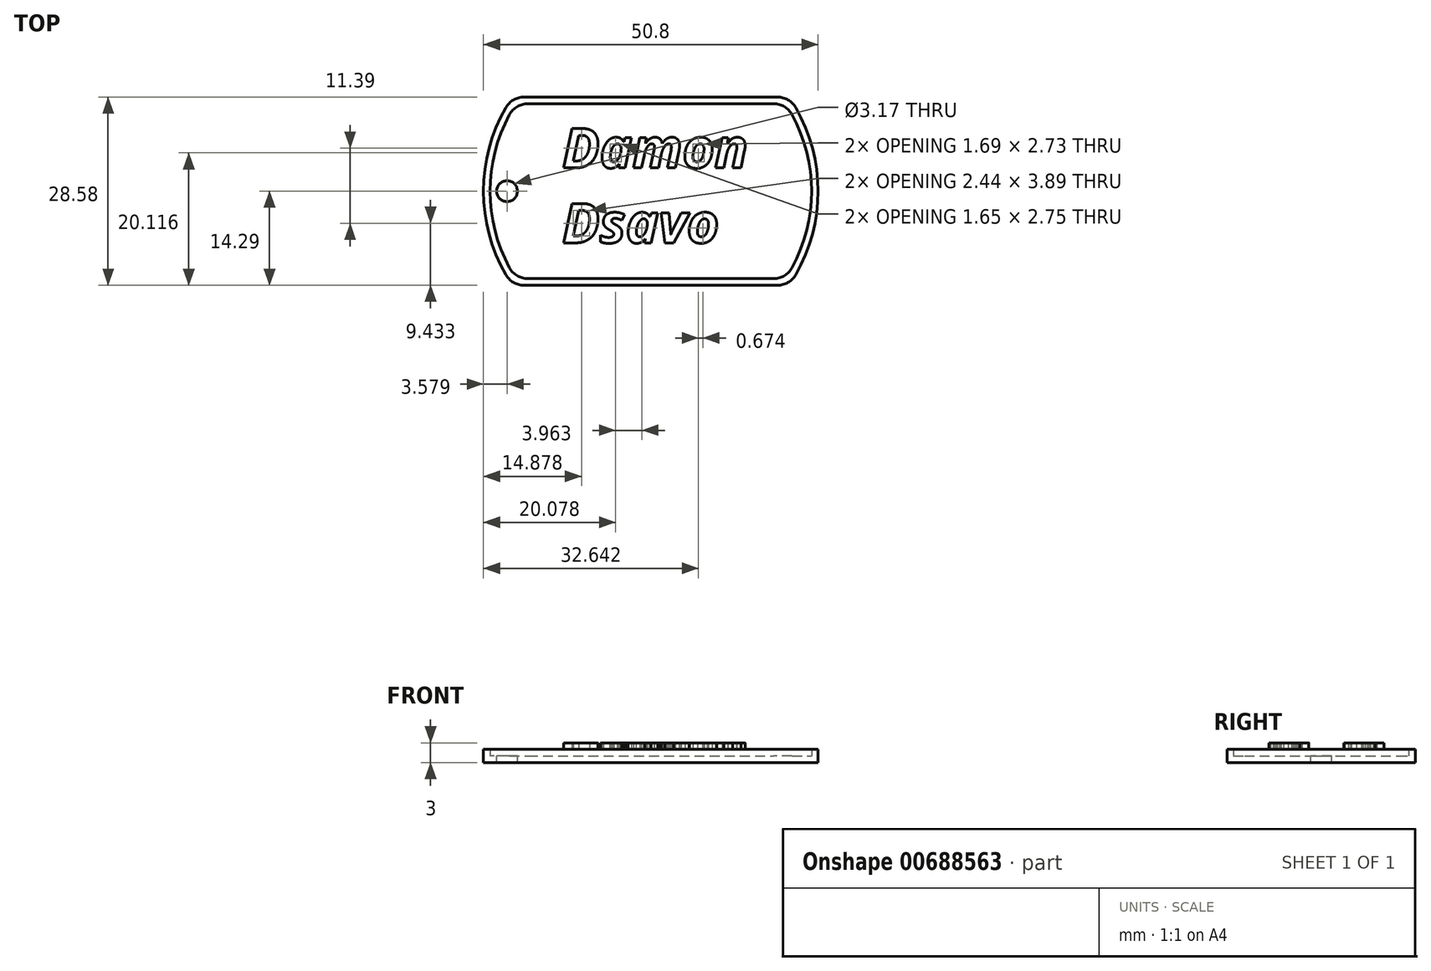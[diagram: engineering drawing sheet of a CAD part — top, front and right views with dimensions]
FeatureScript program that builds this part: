
annotation { "Feature Type Name" : "Feature", "Feature Type Description" : "" }
export const myFeature = defineFeature(function(context is Context, id is Id, definition is map)
    precondition{}
    {
        {
            var Q0;
            Q0=qCreatedBy(makeId("Top.planeOp"),FACE);
            var sketch = newSketch(context, id + "F0", { "sketchPlane" : qUnion([Q0])});
            skArc(sketch, "E0", {"start": v(-22, 12.7) * mm, "mid": v(-25.4, 0) * mm, "end": v(-22, -12.7) * mm});
            skLineSegment(sketch, "E1.top", {"start": v(-19.25, -14.29) * mm, "end": v(19.25, -14.29) * mm});
            skArc(sketch, "E2.trimOffspring", {"start": v(22, -12.7) * mm, "mid": v(25.4, 0) * mm, "end": v(22, 12.7) * mm});
            skLineSegment(sketch, "E3", {"start": v(-19.25, 14.29) * mm, "end": v(19.25, 14.29) * mm});
            skPoint(sketch, "E4.visualSharp", {"position": v(-21, 14.29) * mm});
            skArc(sketch, "E4.filletArc", {"start": v(-19.25, 14.29) * mm, "mid": v(-20.83, 13.86) * mm, "end": v(-22, 12.7) * mm});
            skPoint(sketch, "E5.visualSharp", {"position": v(21, 14.29) * mm});
            skArc(sketch, "E5.filletArc", {"start": v(22, 12.7) * mm, "mid": v(20.83, 13.86) * mm, "end": v(19.25, 14.29) * mm});
            skPoint(sketch, "E6.visualSharp", {"position": v(21, -14.29) * mm});
            skArc(sketch, "E6.filletArc", {"start": v(19.25, -14.29) * mm, "mid": v(20.83, -13.86) * mm, "end": v(22, -12.7) * mm});
            skPoint(sketch, "E7.visualSharp", {"position": v(-21, -14.29) * mm});
            skArc(sketch, "E7.filletArc", {"start": v(-22, -12.7) * mm, "mid": v(-20.83, -13.86) * mm, "end": v(-19.25, -14.29) * mm});
            skSolve(sketch);
        }
        {
            var Q0;
            Q0=makeQuery(id+"F0.imprint","IMPRINT",FACE,{"disambiguationData":[TD([[makeQuery(id+"F0.imprint","IMPRINT",EDGE,{"derivedFrom":sQuery(id+"F0.wireOp",EDGE,"E0")}),1.0]])]});
            extrude(context, id + "F1", {"entities" : qUnion([Q0]), "depth" : 1 * mm, "offsetDistance" : 25.4 * mm});
        }
        {
            var Q0;
            Q0=makeQuery(id+"F1.opExtrude","CAP_FACE",FACE,{"disambiguationData":[OSD([sQuery(id+"F0.wireOp",EDGE,"E0"),sQuery(id+"F0.wireOp",EDGE,"E1.top"),sQuery(id+"F0.wireOp",EDGE,"E2.trimOffspring"),sQuery(id+"F0.wireOp",EDGE,"E3"),sQuery(id+"F0.wireOp",EDGE,"E4.filletArc"),sQuery(id+"F0.wireOp",EDGE,"E5.filletArc"),sQuery(id+"F0.wireOp",EDGE,"E6.filletArc"),sQuery(id+"F0.wireOp",EDGE,"E7.filletArc")])],"isStart":false});
            var sketch = newSketch(context, id + "F2", { "sketchPlane" : qUnion([Q0])});
            skLineSegment(sketch, "E8.0", {"start": v(-18.66, 13.29) * mm, "end": v(18.66, 13.29) * mm});
            skArc(sketch, "E8.1", {"start": v(-21.45, 11.63) * mm, "mid": v(-24.4, 0) * mm, "end": v(-21.45, -11.63) * mm});
            skLineSegment(sketch, "E8.2", {"start": v(-18.66, -13.29) * mm, "end": v(18.66, -13.29) * mm});
            skArc(sketch, "E8.3", {"start": v(21.45, -11.63) * mm, "mid": v(24.4, 0) * mm, "end": v(21.45, 11.63) * mm});
            skPoint(sketch, "E9.visualSharp", {"position": v(-20.46, 13.29) * mm});
            skArc(sketch, "E9.filletArc", {"start": v(-18.66, 13.29) * mm, "mid": v(-20.29, 12.84) * mm, "end": v(-21.45, 11.63) * mm});
            skPoint(sketch, "E10.visualSharp", {"position": v(20.46, 13.29) * mm});
            skArc(sketch, "E10.filletArc", {"start": v(21.45, 11.63) * mm, "mid": v(20.29, 12.84) * mm, "end": v(18.66, 13.29) * mm});
            skPoint(sketch, "E11.visualSharp", {"position": v(20.46, -13.29) * mm});
            skArc(sketch, "E11.filletArc", {"start": v(18.66, -13.29) * mm, "mid": v(20.29, -12.84) * mm, "end": v(21.45, -11.63) * mm});
            skPoint(sketch, "E12.visualSharp", {"position": v(-20.46, -13.29) * mm});
            skArc(sketch, "E12.filletArc", {"start": v(-21.45, -11.63) * mm, "mid": v(-20.29, -12.84) * mm, "end": v(-18.66, -13.29) * mm});
            skLineSegment(sketch, "E13.0", {"start": v(-19.25, 14.29) * mm, "end": v(19.25, 14.29) * mm});
            skArc(sketch, "E13.1", {"start": v(-22, 12.7) * mm, "mid": v(-25.4, 0) * mm, "end": v(-22, -12.7) * mm});
            skLineSegment(sketch, "E13.2", {"start": v(-19.25, -14.29) * mm, "end": v(19.25, -14.29) * mm});
            skArc(sketch, "E13.3", {"start": v(22, -12.7) * mm, "mid": v(25.4, 0) * mm, "end": v(22, 12.7) * mm});
            skPoint(sketch, "E14.visualSharp", {"position": v(-21, -14.29) * mm});
            skArc(sketch, "E14.filletArc", {"start": v(-22, -12.7) * mm, "mid": v(-20.83, -13.86) * mm, "end": v(-19.25, -14.29) * mm});
            skPoint(sketch, "E15.visualSharp", {"position": v(21, -14.29) * mm});
            skArc(sketch, "E15.filletArc", {"start": v(19.25, -14.29) * mm, "mid": v(20.83, -13.86) * mm, "end": v(22, -12.7) * mm});
            skPoint(sketch, "E16.visualSharp", {"position": v(21, 14.29) * mm});
            skArc(sketch, "E16.filletArc", {"start": v(22, 12.7) * mm, "mid": v(20.83, 13.86) * mm, "end": v(19.25, 14.29) * mm});
            skPoint(sketch, "E17.visualSharp", {"position": v(-21, 14.29) * mm});
            skArc(sketch, "E17.filletArc", {"start": v(-19.25, 14.29) * mm, "mid": v(-20.83, 13.86) * mm, "end": v(-22, 12.7) * mm});
            skSolve(sketch);
        }
        {
            var Q0;
            Q0=makeQuery(id+"F2.imprint","IMPRINT",FACE,{"disambiguationData":[TD([[makeQuery(id+"F2.imprint","IMPRINT",EDGE,{"derivedFrom":sQuery(id+"F2.wireOp",EDGE,"E8.0")}),1.0]])]});
            extrude(context, id + "F3", {"entities" : qUnion([Q0]), "operationType" : NewBodyOperationType.ADD, "depth" : 1 * mm, "offsetDistance" : 25.4 * mm});
        }
        {
            var Q0;
            Q0=makeQuery(id+"F1.opExtrude","CAP_FACE",FACE,{"disambiguationData":[OSD([sQuery(id+"F0.wireOp",EDGE,"E0"),sQuery(id+"F0.wireOp",EDGE,"E1.top"),sQuery(id+"F0.wireOp",EDGE,"E2.trimOffspring"),sQuery(id+"F0.wireOp",EDGE,"E3"),sQuery(id+"F0.wireOp",EDGE,"E4.filletArc"),sQuery(id+"F0.wireOp",EDGE,"E5.filletArc"),sQuery(id+"F0.wireOp",EDGE,"E6.filletArc"),sQuery(id+"F0.wireOp",EDGE,"E7.filletArc")])],"isStart":false});
            var sketch = newSketch(context, id + "F4", { "sketchPlane" : qUnion([Q0])});
            skCircle(sketch, "E18", {"center": v(-21.82, 0) * mm, "radius": 1.59 * mm});
            skSolve(sketch);
        }
        {
            var Q0;
            Q0=makeQuery(id+"F4.imprint","IMPRINT",FACE,{"disambiguationData":[TD([[makeQuery(id+"F4.imprint","IMPRINT",EDGE,{"derivedFrom":sQuery(id+"F4.wireOp",EDGE,"E18")}),1.0]])]});
            extrude(context, id + "F5", {"entities" : qUnion([Q0]), "operationType" : NewBodyOperationType.REMOVE, "oppositeDirection" : true, "depth" : 1 * mm, "offsetDistance" : 25.4 * mm});
        }
        {
            var Q0;
            Q0=makeQuery(id+"F3.opExtrude","CAP_FACE",FACE,{"disambiguationData":[OSD([sQuery(id+"F2.wireOp",EDGE,"E8.0"),sQuery(id+"F2.wireOp",EDGE,"E8.1"),sQuery(id+"F2.wireOp",EDGE,"E8.2"),sQuery(id+"F2.wireOp",EDGE,"E8.3"),sQuery(id+"F2.wireOp",EDGE,"E9.filletArc"),sQuery(id+"F2.wireOp",EDGE,"E10.filletArc"),sQuery(id+"F2.wireOp",EDGE,"E11.filletArc"),sQuery(id+"F2.wireOp",EDGE,"E12.filletArc"),sQuery(id+"F2.wireOp",EDGE,"E13.0"),sQuery(id+"F2.wireOp",EDGE,"E13.1"),sQuery(id+"F2.wireOp",EDGE,"E13.2"),sQuery(id+"F2.wireOp",EDGE,"E13.3"),sQuery(id+"F2.wireOp",EDGE,"E14.filletArc"),sQuery(id+"F2.wireOp",EDGE,"E15.filletArc"),sQuery(id+"F2.wireOp",EDGE,"E16.filletArc"),sQuery(id+"F2.wireOp",EDGE,"E17.filletArc")])],"isStart":false});
            var sketch = newSketch(context, id + "F6", { "sketchPlane" : qUnion([Q0])});
            skText(sketch, "E19", { "text": "Damon\nDsavo", "fontName": "OpenSans-BoldItalic.ttf"});
            const initialGuessF6  = {"E19": [-0.01343, 0.00354, 1, 0, 0.00603]};
            skSetInitialGuess(sketch, initialGuessF6);
            skSolve(sketch);
        }
        {
            var Q0;
            Q0 = qSketchRegion(id + "F6", true);
            extrude(context, id + "F7", {"entities" : qUnion([Q0]), "depth" : 1 * mm, "offsetDistance" : 25.4 * mm});
        }
    });
